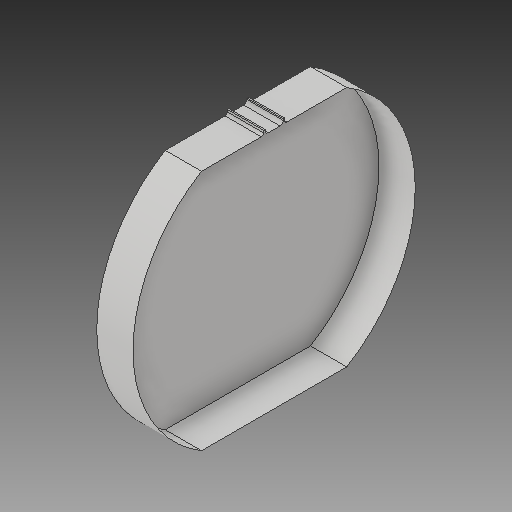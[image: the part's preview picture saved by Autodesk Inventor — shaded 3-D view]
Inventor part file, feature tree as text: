
AUTODESK INVENTOR PART (.ipt)
format: ipt  version: 2017 (Build 210142000, 142)  size: 145,920 bytes
history: native  units: in
note: dims shown in document units (in); Inventor stores cm internally (conversion verified against a paired STEP export)
features: extrude x1, delete_face x1, sketch x1
ambient origin geometry x8: Origin, YZ Plane, XZ Plane, XY Plane, X Axis, Y Axis, Z Axis, Center Point
bodies: Solid2 (feature_tree)
feature tree (3):
  extrude  "connection"  [1 undecoded]
  delete_face  "Delete Face1"
  sketch  "Sketch1"  dims[d12=6.6667in d14=1.0in d15=0.0in d85=4.0in d86=0.5833in d87=3.8873in d88=3.8873in d89=1.7083in d90=0.0625in d91=0.0625in d92=1.6458in d93=0.25in d94=0.125in d96=0.0884in d97=45.0deg d98=3.3333in d99=0.125in]
note: 1 required parameter value undecoded (feature->parameter linkage not recoverable at this tier; creation-order binding heuristic only, values carry confidence <= 0.55)
